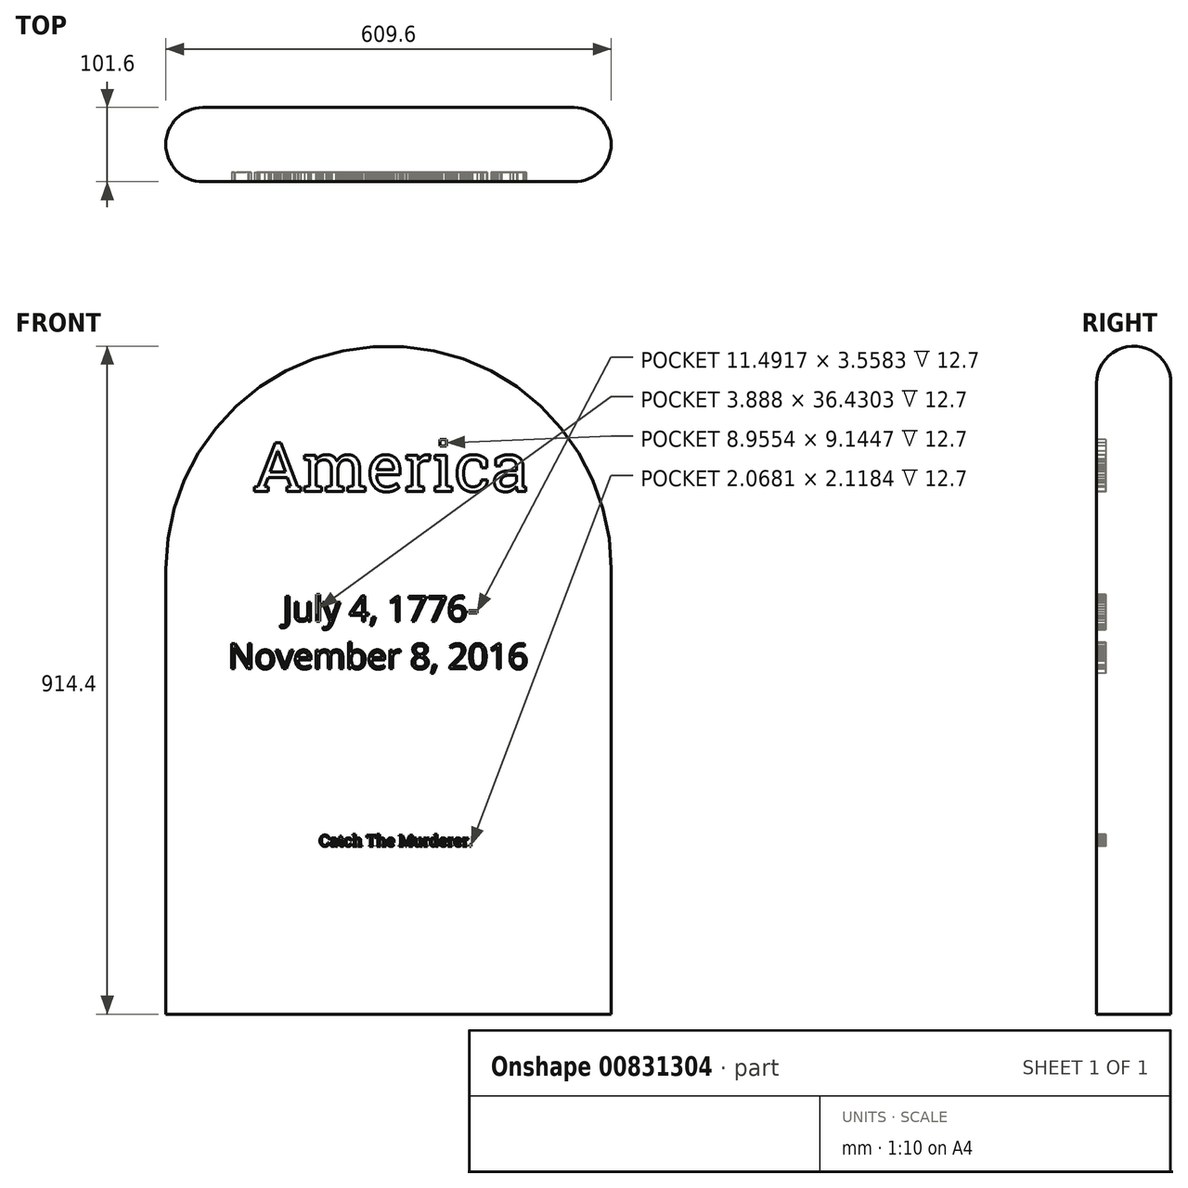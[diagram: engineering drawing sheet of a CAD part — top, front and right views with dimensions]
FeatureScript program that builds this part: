
annotation { "Feature Type Name" : "Feature", "Feature Type Description" : "" }
export const myFeature = defineFeature(function(context is Context, id is Id, definition is map)
    precondition{}
    {
        {
            var Q0;
            Q0=qCreatedBy(makeId("Front.planeOp"),FACE);
            var sketch = newSketch(context, id + "F0", { "sketchPlane" : qUnion([Q0])});
            skLineSegment(sketch, "E0.bottom", {"start": v(0, 0) * mm, "end": v(609.6, 0) * mm});
            skLineSegment(sketch, "E0.left", {"start": v(0, 0) * mm, "end": v(0, 609.6) * mm});
            skLineSegment(sketch, "E0.right", {"start": v(609.6, 0) * mm, "end": v(609.6, 609.6) * mm});
            skArc(sketch, "E1", {"start": v(609.6, 609.6) * mm, "mid": v(304.8, 914.4) * mm, "end": v(0, 609.6) * mm});
            skSolve(sketch);
        }
        {
            var Q0;
            Q0=qSketchRegion(id+"F0",true);
            extrude(context, id + "F1", {"entities" : qUnion([Q0]), "depth" : 101.6 * mm});
        }
        {
            var Q0;
            Q0=makeQuery(id+"F1.opExtrude","CAP_EDGE",EDGE,{"disambiguationData":[OSD([sQuery(id+"F0.wireOp",EDGE,"E1")])],"isStart":false});
            var Q1;
            Q1=makeQuery(id+"F1.opExtrude","CAP_EDGE",EDGE,{"disambiguationData":[OSD([sQuery(id+"F0.wireOp",EDGE,"E1")])],"isStart":true});
            fillet(context, id + "F2", {"entities" : qUnion([Q0, Q1]), "radius" : 50.8 * mm, "tangentPropagation" : true, "allowEdgeOverflow" : false});
        }
        {
            var Q0;
            Q0=makeQuery(id+"F1.opExtrude","CAP_FACE",FACE,{"disambiguationData":[OSD([sQuery(id+"F0.wireOp",EDGE,"E0.bottom"),sQuery(id+"F0.wireOp",EDGE,"E0.left"),sQuery(id+"F0.wireOp",EDGE,"E0.right"),sQuery(id+"F0.wireOp",EDGE,"E1")])],"isStart":false});
            var sketch = newSketch(context, id + "F3", { "sketchPlane" : qUnion([Q0])});
            skText(sketch, "E2", { "text": "America", "fontName": "RobotoSlab-Regular.ttf"});
            skText(sketch, "E3", { "text": "      July 4, 1776-\nNovember 8, 2016", "fontName": "OpenSans-Regular.ttf"});
            skText(sketch, "E4", { "text": "Catch The Murderer.", "fontName": "RobotoSlab-Regular.ttf"});
            const initialGuessF3  = {"E2": [0.11902, 0.71571, 1, 0, 0.0671], "E3": [0.0855, 0.5378, 1, 0, 0.03452], "E4": [0.21017, 0.22974, 1, 0, 0.01547]};
            skSetInitialGuess(sketch, initialGuessF3);
            skSolve(sketch);
        }
        {
            var Q0;
            Q0=qSketchRegion(id+"F3",true);
            extrude(context, id + "F4", {"entities" : qUnion([Q0]), "operationType" : NewBodyOperationType.REMOVE, "oppositeDirection" : true, "depth" : 12.7 * mm});
        }
    });
